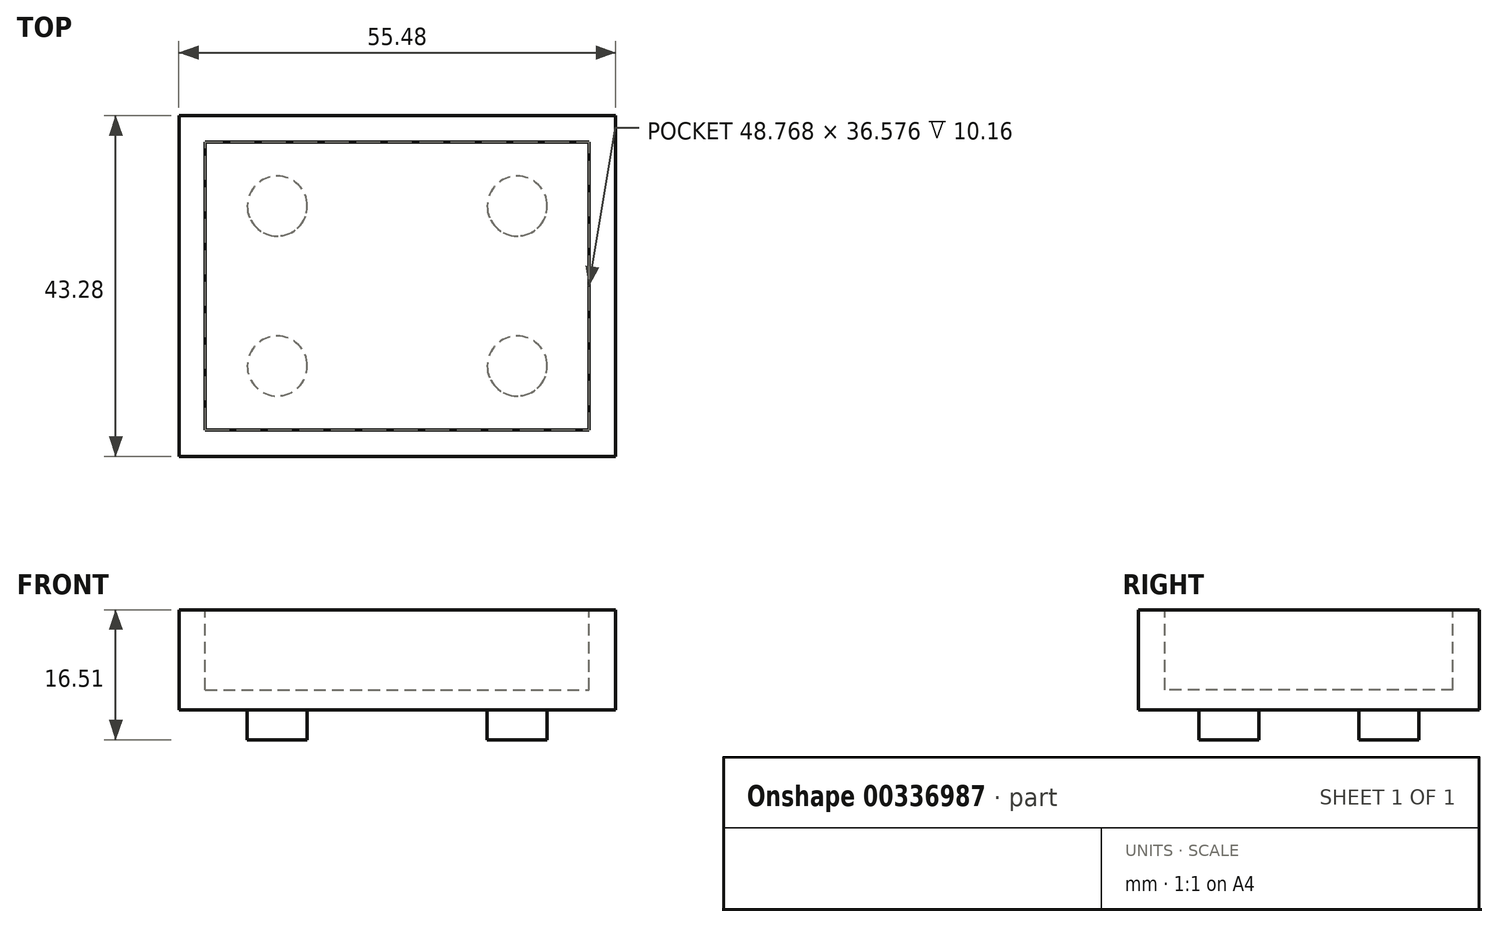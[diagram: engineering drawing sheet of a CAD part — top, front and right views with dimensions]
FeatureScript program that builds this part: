
annotation { "Feature Type Name" : "Feature", "Feature Type Description" : "" }
export const myFeature = defineFeature(function(context is Context, id is Id, definition is map)
    precondition{}
    {
        {
            var Q0;
            Q0=qCreatedBy(makeId("Top.planeOp"),FACE);
            var sketch = newSketch(context, id + "F0", { "sketchPlane" : qUnion([Q0])});
            skLineSegment(sketch, "E0.bottom", {"start": v(-27.74, 21.64) * mm, "end": v(27.74, 21.64) * mm});
            skLineSegment(sketch, "E0.top", {"start": v(-27.74, -21.64) * mm, "end": v(27.74, -21.64) * mm});
            skLineSegment(sketch, "E0.left", {"start": v(-27.74, 21.64) * mm, "end": v(-27.74, -21.64) * mm});
            skLineSegment(sketch, "E0.right", {"start": v(27.74, 21.64) * mm, "end": v(27.74, -21.64) * mm});
            skSolve(sketch);
        }
        {
            var Q0;
            Q0=makeQuery(id+"F0.imprint","IMPRINT",FACE,{"disambiguationData":[TD([[makeQuery(id+"F0.imprint","IMPRINT",EDGE,{"derivedFrom":sQuery(id+"F0.wireOp",EDGE,"E0.bottom")}),-1.0]])]});
            extrude(context, id + "F1", {"entities" : qUnion([Q0]), "depth" : 12.7 * mm});
        }
        {
            var Q0;
            Q0=makeQuery(id+"F1.opExtrude","CAP_FACE",FACE,{"disambiguationData":[OSD([sQuery(id+"F0.wireOp",EDGE,"E0.bottom"),sQuery(id+"F0.wireOp",EDGE,"E0.top"),sQuery(id+"F0.wireOp",EDGE,"E0.left"),sQuery(id+"F0.wireOp",EDGE,"E0.right")])],"isStart":false});
            var sketch = newSketch(context, id + "F2", { "sketchPlane" : qUnion([Q0])});
            skLineSegment(sketch, "E1.bottom", {"start": v(-24.38, 18.29) * mm, "end": v(24.38, 18.29) * mm});
            skLineSegment(sketch, "E1.top", {"start": v(-24.38, -18.29) * mm, "end": v(24.38, -18.29) * mm});
            skLineSegment(sketch, "E1.left", {"start": v(-24.38, 18.29) * mm, "end": v(-24.38, -18.29) * mm});
            skLineSegment(sketch, "E1.right", {"start": v(24.38, 18.29) * mm, "end": v(24.38, -18.29) * mm});
            skSolve(sketch);
        }
        {
            var Q0;
            Q0=makeQuery(id+"F2.imprint","IMPRINT",FACE,{"disambiguationData":[TD([[makeQuery(id+"F2.imprint","IMPRINT",EDGE,{"derivedFrom":sQuery(id+"F2.wireOp",EDGE,"E1.bottom")}),-1.0]])]});
            var Q1;
            {var subQ0=sQuery(id+"F2.wireOp",EDGE,"xE66SGNx-GrgY-PejV-YlqO-G6TC2m1s6DQk");Q1=makeQuery(id+"F2.imprint","IMPRINT",FACE,{"disambiguationData":[TD([[makeQuery(id+"F2.imprint","IMPRINT",EDGE,{"derivedFrom":subQ0}),1.0]])]});}
            var Q2;
            {var subQ0=sQuery(id+"F2.wireOp",EDGE,"hloqKAMS-Yv4F-IQRk-kITP-7j438E4D0vCP");Q2=makeQuery(id+"F2.imprint","IMPRINT",FACE,{"disambiguationData":[TD([[makeQuery(id+"F2.imprint","IMPRINT",EDGE,{"derivedFrom":subQ0}),1.0]])]});}
            var Q3;
            Q3=makeQuery(id+"F2.imprint","IMPRINT",FACE,{"disambiguationData":[TD([[makeQuery(id+"F2.imprint","IMPRINT",EDGE,{"derivedFrom":sQuery(id+"F2.wireOp",EDGE,"QqfkbW2t-ikMu-UeDE-00UW-P9dejG2vY9fJ.bottom")}),-1.0]])]});
            extrude(context, id + "F3", {"entities" : qUnion([Q0, Q1, Q2, Q3]), "operationType" : NewBodyOperationType.REMOVE, "oppositeDirection" : true, "depth" : 10.16 * mm});
        }
        {
            var Q0;
            Q0=makeQuery(id+"F1.opExtrude","CAP_FACE",FACE,{"disambiguationData":[OSD([sQuery(id+"F0.wireOp",EDGE,"E0.bottom"),sQuery(id+"F0.wireOp",EDGE,"E0.top"),sQuery(id+"F0.wireOp",EDGE,"E0.left"),sQuery(id+"F0.wireOp",EDGE,"E0.right")])],"isStart":true});
            var sketch = newSketch(context, id + "F4", { "sketchPlane" : qUnion([Q0])});
            skCircle(sketch, "E2", {"center": v(-15.24, 10.16) * mm, "radius": 3.81 * mm});
            skCircle(sketch, "E3", {"center": v(15.24, 10.16) * mm, "radius": 3.81 * mm});
            skCircle(sketch, "E4", {"center": v(-15.24, -10.16) * mm, "radius": 3.81 * mm});
            skCircle(sketch, "E5", {"center": v(15.24, -10.16) * mm, "radius": 3.81 * mm});
            skSolve(sketch);
        }
        {
            var Q0;
            Q0=makeQuery(id+"F4.imprint","IMPRINT",FACE,{"disambiguationData":[TD([[makeQuery(id+"F4.imprint","IMPRINT",EDGE,{"derivedFrom":sQuery(id+"F4.wireOp",EDGE,"E5")}),1.0]])]});
            var Q1;
            Q1=makeQuery(id+"F4.imprint","IMPRINT",FACE,{"disambiguationData":[TD([[makeQuery(id+"F4.imprint","IMPRINT",EDGE,{"derivedFrom":sQuery(id+"F4.wireOp",EDGE,"E4")}),1.0]])]});
            var Q2;
            Q2=makeQuery(id+"F4.imprint","IMPRINT",FACE,{"disambiguationData":[TD([[makeQuery(id+"F4.imprint","IMPRINT",EDGE,{"derivedFrom":sQuery(id+"F4.wireOp",EDGE,"E3")}),1.0]])]});
            var Q3;
            Q3=makeQuery(id+"F4.imprint","IMPRINT",FACE,{"disambiguationData":[TD([[makeQuery(id+"F4.imprint","IMPRINT",EDGE,{"derivedFrom":sQuery(id+"F4.wireOp",EDGE,"E2")}),1.0]])]});
            extrude(context, id + "F5", {"entities" : qUnion([Q0, Q1, Q2, Q3]), "operationType" : NewBodyOperationType.ADD, "depth" : 3.8 * mm});
        }
    });
